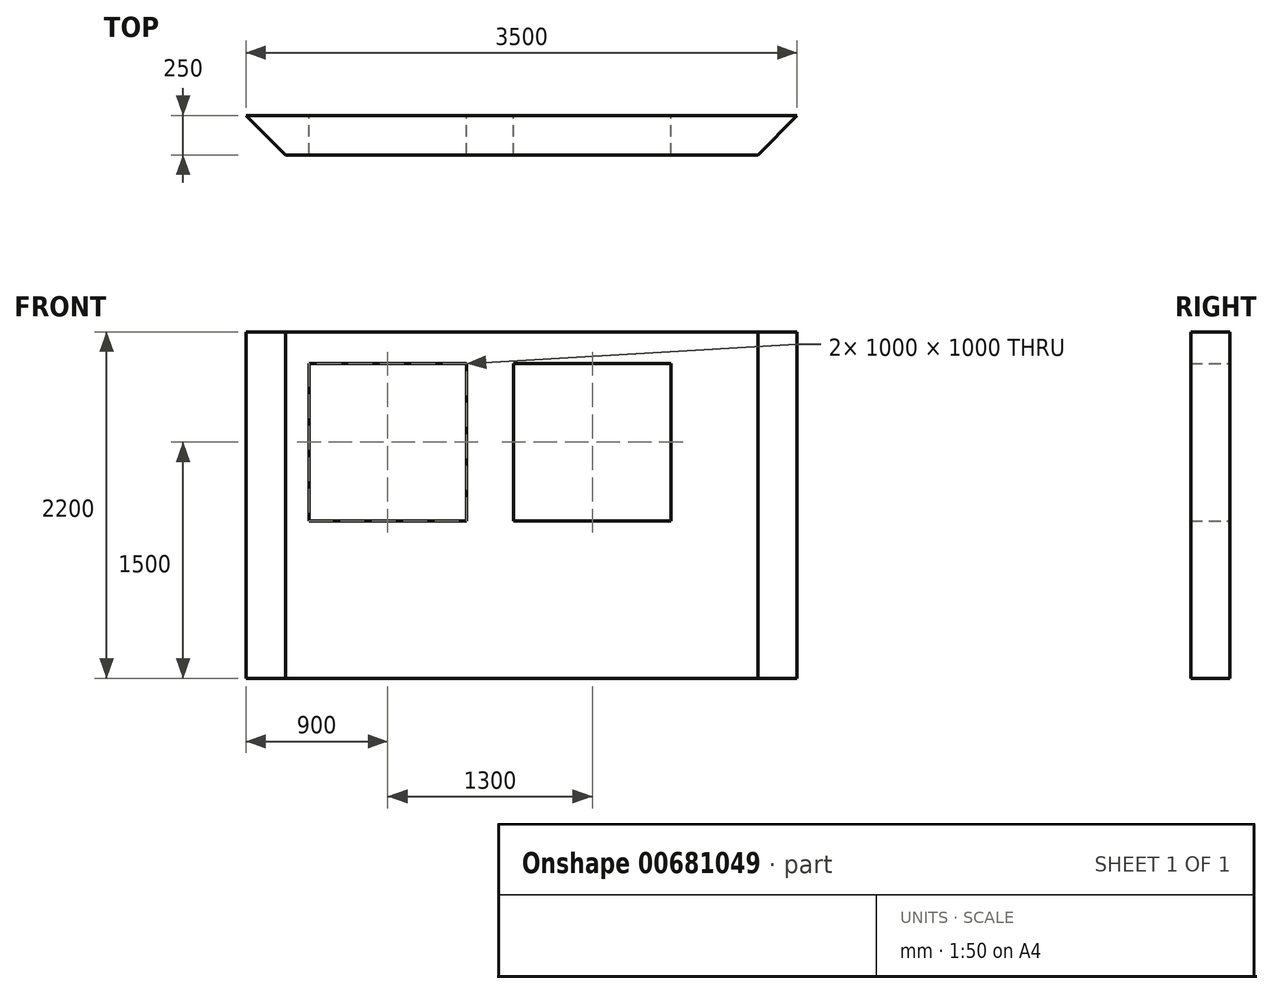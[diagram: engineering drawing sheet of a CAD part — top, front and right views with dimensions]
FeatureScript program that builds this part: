
annotation { "Feature Type Name" : "Feature", "Feature Type Description" : "" }
export const myFeature = defineFeature(function(context is Context, id is Id, definition is map)
    precondition{}
    {
        {
            var Q0;
            Q0=qCreatedBy(makeId("Front.planeOp"),FACE);
            var sketch = newSketch(context, id + "F0", { "sketchPlane" : qUnion([Q0])});
            skLineSegment(sketch, "E0.bottom", {"start": v(0, 0) * mm, "end": v(3500, 0) * mm});
            skLineSegment(sketch, "E0.top", {"start": v(0, 2200) * mm, "end": v(3500, 2200) * mm});
            skLineSegment(sketch, "E0.left", {"start": v(0, 0) * mm, "end": v(0, 2200) * mm});
            skLineSegment(sketch, "E0.right", {"start": v(3500, 0) * mm, "end": v(3500, 2200) * mm});
            skSolve(sketch);
        }
        {
            var Q0;
            Q0 = qSketchRegion(id + "F0", true);
            extrude(context, id + "F1", {"entities" : qUnion([Q0]), "depth" : 250 * mm, "offsetDistance" : 25 * mm});
        }
        {
            var Q0;
            Q0=makeQuery(id+"F1.opExtrude","SWEPT_FACE",FACE,{"disambiguationData":[OSD([sQuery(id+"F0.wireOp",EDGE,"E0.top")])]});
            var sketch = newSketch(context, id + "F2", { "sketchPlane" : qUnion([Q0])});
            skLineSegment(sketch, "E1", {"start": v(0, 0) * mm, "end": v(250, -250) * mm});
            skLineSegment(sketch, "E2", {"start": v(250, -250) * mm, "end": v(0, -250) * mm});
            skLineSegment(sketch, "E3", {"start": v(0, -250) * mm, "end": v(0, 0) * mm});
            skLineSegment(sketch, "E4", {"start": v(3500, -250) * mm, "end": v(3250, -250) * mm});
            skLineSegment(sketch, "E5", {"start": v(3250, -250) * mm, "end": v(3500, 0) * mm});
            skLineSegment(sketch, "E6", {"start": v(3500, 0) * mm, "end": v(3500, -250) * mm});
            skLineSegment(sketch, "E7", {"start": v(1750, -250) * mm, "end": v(1750, 0) * mm, "construction": true});
            skSolve(sketch);
        }
        {
            var Q0;
            Q0 = qSketchRegion(id + "F2", true);
            extrude(context, id + "F3", {"entities" : qUnion([Q0]), "operationType" : NewBodyOperationType.REMOVE, "endBound" : BoundingType.THROUGH_ALL, "oppositeDirection" : true, "depth" : 25 * mm, "offsetDistance" : 25 * mm});
        }
        {
            var Q0;
            Q0=makeQuery(id+"F1.opExtrude","CAP_FACE",FACE,{"disambiguationData":[OSD([sQuery(id+"F0.wireOp",EDGE,"E0.bottom"),sQuery(id+"F0.wireOp",EDGE,"E0.top"),sQuery(id+"F0.wireOp",EDGE,"E0.left"),sQuery(id+"F0.wireOp",EDGE,"E0.right")])],"isStart":true});
            var sketch = newSketch(context, id + "F4", { "sketchPlane" : qUnion([Q0])});
            skLineSegment(sketch, "E8.bottom", {"start": v(-2700, 1000) * mm, "end": v(-1700, 1000) * mm});
            skLineSegment(sketch, "E8.top", {"start": v(-2700, 2000) * mm, "end": v(-1700, 2000) * mm});
            skLineSegment(sketch, "E8.left", {"start": v(-2700, 1000) * mm, "end": v(-2700, 2000) * mm});
            skLineSegment(sketch, "E8.right", {"start": v(-1700, 1000) * mm, "end": v(-1700, 2000) * mm});
            skLineSegment(sketch, "E9.bottom", {"start": v(-1400, 2000) * mm, "end": v(-400, 2000) * mm});
            skLineSegment(sketch, "E9.top", {"start": v(-1400, 1000) * mm, "end": v(-400, 1000) * mm});
            skLineSegment(sketch, "E9.left", {"start": v(-1400, 2000) * mm, "end": v(-1400, 1000) * mm});
            skLineSegment(sketch, "E9.right", {"start": v(-400, 2000) * mm, "end": v(-400, 1000) * mm});
            skLineSegment(sketch, "E10", {"start": v(-1700, 1000) * mm, "end": v(-1400, 1000) * mm, "construction": true});
            skSolve(sketch);
        }
        {
            var Q0;
            Q0 = qSketchRegion(id + "F4", true);
            extrude(context, id + "F5", {"entities" : qUnion([Q0]), "operationType" : NewBodyOperationType.REMOVE, "endBound" : BoundingType.THROUGH_ALL, "oppositeDirection" : true, "depth" : 25 * mm, "offsetDistance" : 25 * mm});
        }
    });
